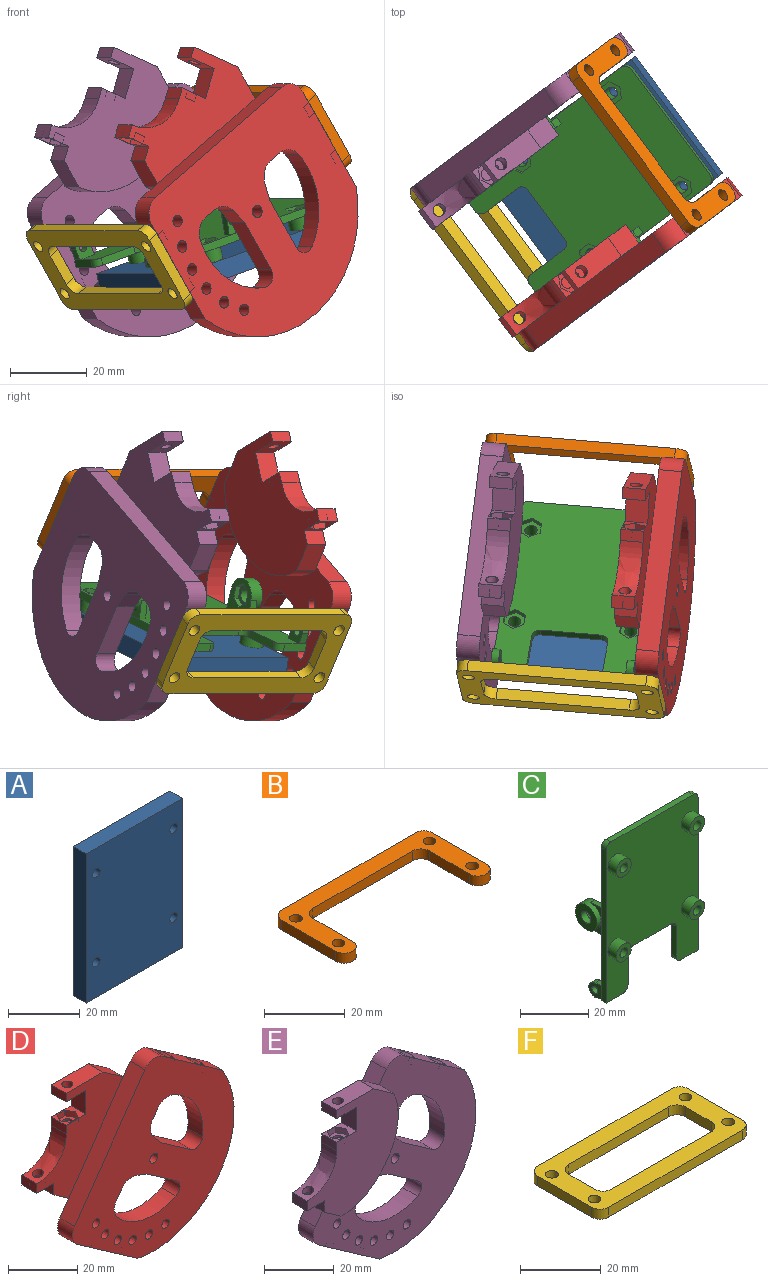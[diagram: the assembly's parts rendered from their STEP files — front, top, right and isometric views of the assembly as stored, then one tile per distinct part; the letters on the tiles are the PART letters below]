
ASSEMBLY  parts=6 mates=5
PART A: 10 faces, bbox 38x5x51 mm
  f0: plane 38x5mm, normal (0,0,1), area 190mm2, adj f1,f7,f8,f9
  f1: plane 51x5mm, normal (-1,0,0), area 255mm2, adj f0,f2,f8,f9
  f2: plane 38x5mm, normal (0,0,-1), area 190mm2, adj f1,f7,f8,f9
  f3: cylinder r=1.5mm len=5mm, axis (0,1,0), area 47.1mm2, adj f8,f9
  f4: cylinder r=1.5mm len=5mm, axis (0,1,0), area 47.1mm2, adj f8,f9
  f5: cylinder r=1.5mm len=5mm, axis (0,1,0), area 47.1mm2, adj f8,f9
  f6: cylinder r=1.5mm len=5mm, axis (0,1,0), area 47.1mm2, adj f8,f9
  f7: plane 51x5mm, normal (1,0,0), area 255mm2, adj f0,f2,f8,f9
  f8: plane 51x38mm, normal (0,-1,0), area 1909.7mm2, adj f0,f1,f2,f3,f4,f5,f6,f7
  f9: plane 51x38mm, normal (0,1,0), area 1909.7mm2, adj f0,f1,f2,f3,f4,f5,f6,f7
PART B: 18 faces, bbox 53x25x3 mm
  f0: cylinder r=3mm len=6mm, axis (0,0,-1), area 28.3mm2, adj f1,f15,f16,f17
  f1: plane 19x3mm, normal (1,0,0), area 57mm2, adj f0,f2,f16,f17
  f2: cylinder r=3mm len=3mm, axis (0,0,-1), area 14.1mm2, adj f1,f3,f16,f17
  f3: plane 47x3mm, normal (0,1,0), area 141mm2, adj f2,f4,f16,f17
  f4: cylinder r=3mm len=3mm, axis (0,0,-1), area 14.1mm2, adj f3,f5,f16,f17
  f5: plane 19x3mm, normal (-1,0,0), area 57mm2, adj f4,f6,f16,f17
  f6: cylinder r=3mm len=6mm, axis (0,0,-1), area 28.3mm2, adj f5,f7,f16,f17
  f7: plane 14x3mm, normal (1,0,0), area 42mm2, adj f6,f8,f16,f17
  f8: cylinder r=3mm len=3mm, axis (0,0,-1), area 14.1mm2, adj f7,f9,f16,f17
  f9: plane 35x3mm, normal (0,-1,0), area 105mm2, adj f8,f10,f16,f17
  f10: cylinder r=3mm len=3mm, axis (0,0,-1), area 14.1mm2, adj f9,f15,f16,f17
  f11: cylinder r=1.6mm len=3.2mm, axis (0,0,-1), area 30.2mm2, adj f16,f17
  f12: cylinder r=1.6mm len=3.2mm, axis (0,0,-1), area 30.2mm2, adj f16,f17
  f13: cylinder r=1.6mm len=3.2mm, axis (0,0,-1), area 30.2mm2, adj f16,f17
  f14: cylinder r=1.6mm len=3.2mm, axis (0,0,-1), area 30.2mm2, adj f16,f17
  f15: plane 14x3mm, normal (-1,0,0), area 42mm2, adj f0,f10,f16,f17
  f16: plane 53x25mm, normal (0,0,1), area 465.1mm2, adj f0,f1,f2,f3,f4,f5,f6,f7
  f17: plane 53x25mm, normal (0,0,-1), area 465.1mm2, adj f0,f1,f2,f3,f4,f5,f6,f7
PART C: 98 faces, bbox 40.8x15x57.5 mm
  f0: plane 7.1x2mm, normal (0,0,-1), area 14.2mm2, adj f1,f2,f7,f74,f94
  f1: plane 57x38.2mm, normal (0,1,0), area 1713.4mm2, adj f0,f3,f4,f6,f7,f8,f22,f23
  f2: plane 57x38.2mm, normal (0,-1,0), area 1754.9mm2, adj f0,f6,f7,f8,f13,f15,f17,f19
  f3: plane 10x5mm, normal (1,0,0), area 15.7mm2, adj f1,f21,f22,f23
  f4: plane 5.54x5.5mm, normal (1,0,0), area 20mm2, adj f1,f25,f26,f27,f28,f29
  f5: cylinder r=2mm len=4mm, axis (1,0,0), area 27mm2, adj f31,f32
  f6: plane 34.2x2mm, normal (0,0,1), area 68.4mm2, adj f1,f2,f96,f97
  f7: plane 55x2mm, normal (-1,0,0), area 110mm2, adj f0,f1,f2,f97
  f8: plane 7.1x2mm, normal (0,0,-1), area 14.2mm2, adj f1,f2,f28,f67,f95
  f9: cylinder r=1.6mm len=4.35mm, axis (0,1,0), area 43.7mm2, adj f20,f54
  f10: cylinder r=1.6mm len=4.35mm, axis (0,1,0), area 43.7mm2, adj f14,f50
  f11: cylinder r=1.6mm len=4.35mm, axis (0,1,0), area 43.7mm2, adj f16,f46
  f12: cylinder r=1.6mm len=4.35mm, axis (0,1,0), area 43.7mm2, adj f18,f42
  f13: cylinder r=3.1mm len=6.2mm, axis (0,1,0), area 68.2mm2, adj f2,f14
  f14: plane 6.2x6.2mm, normal (0,-1,0), area 22.1mm2, adj f10,f13
  f15: cylinder r=3.1mm len=6.2mm, axis (0,1,0), area 68.2mm2, adj f2,f16
  f16: plane 6.2x6.2mm, normal (0,-1,0), area 22.1mm2, adj f11,f15
  f17: cylinder r=3.1mm len=6.2mm, axis (0,1,0), area 68.2mm2, adj f2,f18
  f18: plane 6.2x6.2mm, normal (0,-1,0), area 22.1mm2, adj f12,f17
  f19: cylinder r=3.1mm len=6.2mm, axis (0,1,0), area 68.2mm2, adj f2,f20
  f20: plane 6.2x6.2mm, normal (0,-1,0), area 22.1mm2, adj f9,f19
  f21: cylinder r=4.5mm len=9mm, axis (1,0,0), area 74.9mm2, adj f3,f22,f23,f24,f31
  f22: plane 5x2mm, normal (0,0.1,1), area 10mm2, adj f1,f3,f21,f24
  f23: plane 5x2mm, normal (0,0.1,-1), area 10mm2, adj f1,f3,f21,f24
  f24: plane 10x9.5mm, normal (-1,0,0), area 53.1mm2, adj f1,f21,f22,f23,f33,f34,f35,f36
  f25: plane 2x0.04mm, normal (0,1,0), area 0.1mm2, adj f4,f26,f28,f30
  f26: cylinder r=2.5mm len=5mm, axis (1,0,0), area 15.7mm2, adj f4,f25,f27,f30
  f27: plane 3x2mm, normal (0,0.16,0.99), area 6.1mm2, adj f1,f4,f26,f30
  f28: plane 3x2mm, normal (0,-0.18,-0.98), area 6.1mm2, adj f4,f8,f25,f30
  f29: cylinder r=1.25mm len=2.5mm, axis (1,0,0), area 15.7mm2, adj f4,f30
  f30: plane 5.54x5.5mm, normal (-1,0,0), area 20mm2, adj f1,f25,f26,f27,f28,f29
  f31: plane 9x9mm, normal (1,0,0), area 51.1mm2, adj f5,f21
  f32: plane 6.35x5.5mm, normal (-1,0,0), area 13.6mm2, adj f5,f33,f34,f35,f36,f37,f38
  f33: plane 3.18x1.5mm, normal (0,0,1), area 4.8mm2, adj f24,f32,f34,f38
  f34: plane 2.75x1.59mm, normal (0,0.87,0.5), area 4.8mm2, adj f24,f32,f33,f35
  f35: plane 2.75x1.59mm, normal (0,0.87,-0.5), area 4.8mm2, adj f24,f32,f34,f36
  f36: plane 3.18x1.5mm, normal (0,0,-1), area 4.8mm2, adj f24,f32,f35,f37
  f37: plane 2.75x1.59mm, normal (0,-0.87,-0.5), area 4.8mm2, adj f24,f32,f36,f38
  f38: plane 2.75x1.59mm, normal (0,-0.87,0.5), area 4.8mm2, adj f24,f32,f33,f37
  f39: plane 2.7x1.56mm, normal (0.5,0,-0.87), area 3.6mm2, adj f1,f40,f42,f66
  f40: plane 3.18x1.15mm, normal (1,0,0), area 3.7mm2, adj f1,f39,f41,f42
  f41: plane 2.7x1.56mm, normal (0.5,0,0.87), area 3.6mm2, adj f1,f40,f42,f65
  f42: plane 6.29x5.4mm, normal (0,1,0), area 17.5mm2, adj f12,f39,f40,f41,f64,f65,f66
  f43: plane 2.7x1.56mm, normal (0.5,0,-0.87), area 3.6mm2, adj f1,f44,f46,f63
  f44: plane 3.18x1.15mm, normal (1,0,0), area 3.7mm2, adj f1,f43,f45,f46
  f45: plane 2.7x1.56mm, normal (0.5,0,0.87), area 3.6mm2, adj f1,f44,f46,f62
  f46: plane 6.29x5.4mm, normal (0,1,0), area 17.5mm2, adj f11,f43,f44,f45,f61,f62,f63
  f47: plane 2.7x1.56mm, normal (0.5,0,0.87), area 3.6mm2, adj f1,f49,f50,f60
  f48: plane 2.7x1.56mm, normal (0.5,0,-0.87), area 3.6mm2, adj f1,f49,f50,f59
  f49: plane 3.18x1.15mm, normal (1,0,0), area 3.7mm2, adj f1,f47,f48,f50
  f50: plane 6.29x5.4mm, normal (0,1,0), area 17.5mm2, adj f10,f47,f48,f49,f58,f59,f60
  f51: plane 2.7x1.56mm, normal (0.5,0,-0.87), area 3.6mm2, adj f1,f52,f54,f57
  f52: plane 3.18x1.15mm, normal (1,0,0), area 3.7mm2, adj f1,f51,f53,f54
  f53: plane 2.7x1.56mm, normal (0.5,0,0.87), area 3.6mm2, adj f1,f52,f54,f56
  f54: plane 6.29x5.4mm, normal (0,1,0), area 17.5mm2, adj f9,f51,f52,f53,f55,f56,f57
  f55: plane 3.18x1.15mm, normal (-1,0,0), area 3.7mm2, adj f1,f54,f56,f57
  f56: plane 2.7x1.56mm, normal (-0.5,0,0.87), area 3.6mm2, adj f1,f53,f54,f55
  f57: plane 2.7x1.56mm, normal (-0.5,0,-0.87), area 3.6mm2, adj f1,f51,f54,f55
  f58: plane 3.18x1.15mm, normal (-1,0,0), area 3.7mm2, adj f1,f50,f59,f60
  f59: plane 2.7x1.56mm, normal (-0.5,0,-0.87), area 3.6mm2, adj f1,f48,f50,f58
  f60: plane 2.7x1.56mm, normal (-0.5,0,0.87), area 3.6mm2, adj f1,f47,f50,f58
  f61: plane 3.18x1.15mm, normal (-1,0,0), area 3.7mm2, adj f1,f46,f62,f63
  f62: plane 2.7x1.56mm, normal (-0.5,0,0.87), area 3.6mm2, adj f1,f45,f46,f61
  f63: plane 2.7x1.56mm, normal (-0.5,0,-0.87), area 3.6mm2, adj f1,f43,f46,f61
  f64: plane 3.18x1.15mm, normal (-1,0,0), area 3.7mm2, adj f1,f42,f65,f66
  f65: plane 2.7x1.56mm, normal (-0.5,0,0.87), area 3.6mm2, adj f1,f41,f42,f64
  f66: plane 2.7x1.56mm, normal (-0.5,0,-0.87), area 3.6mm2, adj f1,f39,f42,f64
  f67: plane 55x2mm, normal (1,0,0), area 110mm2, adj f1,f2,f8,f96
  f68: plane 2x0.04mm, normal (0,1,0), area 0.1mm2, adj f70,f72,f73,f74
  f69: cylinder r=1.25mm len=2.5mm, axis (-1,0,0), area 15.7mm2, adj f72,f73
  f70: cylinder r=2.5mm len=5mm, axis (-1,0,0), area 15.7mm2, adj f68,f71,f72,f73
  f71: plane 3x2mm, normal (0,0.16,0.99), area 6.1mm2, adj f1,f70,f72,f73
  f72: plane 5.54x5.5mm, normal (-1,0,0), area 20mm2, adj f1,f68,f69,f70,f71,f74
  f73: plane 5.54x5.5mm, normal (1,0,0), area 20mm2, adj f1,f68,f69,f70,f71,f74
  f74: plane 3x2mm, normal (0,-0.18,-0.98), area 6.1mm2, adj f0,f68,f72,f73
  f75: plane 10x5mm, normal (-1,0,0), area 15.7mm2, adj f1,f77,f78,f79
  f76: cylinder r=2mm len=4mm, axis (-1,0,0), area 27mm2, adj f81,f82
  f77: cylinder r=4.5mm len=9mm, axis (-1,0,0), area 74.9mm2, adj f75,f78,f79,f80,f81
  f78: plane 5x2mm, normal (0,0.1,1), area 10mm2, adj f1,f75,f77,f80
  f79: plane 5x2mm, normal (0,0.1,-1), area 10mm2, adj f1,f75,f77,f80
  f80: plane 10x9.5mm, normal (1,0,0), area 53.1mm2, adj f1,f77,f78,f79,f83,f84,f85,f86
  f81: plane 9x9mm, normal (-1,0,0), area 51.1mm2, adj f76,f77
  f82: plane 6.35x5.5mm, normal (1,0,0), area 13.6mm2, adj f76,f83,f84,f85,f86,f87,f88
  f83: plane 3.18x1.5mm, normal (0,0,1), area 4.8mm2, adj f80,f82,f84,f88
  f84: plane 2.75x1.59mm, normal (0,0.87,0.5), area 4.8mm2, adj f80,f82,f83,f85
  f85: plane 2.75x1.59mm, normal (0,0.87,-0.5), area 4.8mm2, adj f80,f82,f84,f86
  f86: plane 3.18x1.5mm, normal (0,0,-1), area 4.8mm2, adj f80,f82,f85,f87
  f87: plane 2.75x1.59mm, normal (0,-0.87,-0.5), area 4.8mm2, adj f80,f82,f86,f88
  f88: plane 2.75x1.59mm, normal (0,-0.87,0.5), area 4.8mm2, adj f80,f82,f83,f87
  f89: cylinder r=2mm len=2mm, axis (0,1,0), area 6.3mm2, adj f1,f2,f90,f93
  f90: plane 11x2mm, normal (1,0,0), area 22mm2, adj f1,f2,f89,f94
  f91: plane 11x2mm, normal (-1,0,0), area 22mm2, adj f1,f2,f92,f95
  f92: cylinder r=2mm len=2mm, axis (0,1,0), area 6.3mm2, adj f1,f2,f91,f93
  f93: plane 16x2mm, normal (0,0,-1), area 32mm2, adj f1,f2,f89,f92
  f94: cylinder r=2mm len=2mm, axis (0,-1,0), area 6.3mm2, adj f0,f1,f2,f90
  f95: cylinder r=2mm len=2mm, axis (0,1,0), area 6.3mm2, adj f1,f2,f8,f91
  f96: cylinder r=2mm len=2mm, axis (0,-1,0), area 6.3mm2, adj f1,f2,f6,f67
  f97: cylinder r=2mm len=2mm, axis (0,-1,0), area 6.3mm2, adj f1,f2,f6,f7
PART D: 90 faces, bbox 74.4x12x67.9 mm
  f0: cylinder r=1.6mm len=3.2mm, axis (0,0,-1), area 19mm2, adj f6,f55
  f1: plane 37.48x35.19mm, normal (0,-1,0), area 524.2mm2, adj f2,f3,f4,f5,f6,f7,f8,f9
  f2: plane 8x6mm, normal (0,0,-1), area 40mm2, adj f1,f3,f14,f15,f45
  f3: plane 8.3x6mm, normal (-1,0,0), area 49.8mm2, adj f1,f2,f4,f15
  f4: plane 8x6mm, normal (0,0,1), area 21.8mm2, adj f1,f3,f5,f15,f47,f48,f49,f50
  f5: plane 6x3mm, normal (-1,0,0), area 18mm2, adj f1,f4,f6,f15
  f6: extruded ~12x11.61mm, area 103.6mm2, adj f0,f1,f5,f7,f15
  f7: plane 6x3.45mm, normal (-1,0,0), area 20.7mm2, adj f1,f6,f8,f15
  f8: plane 7x6mm, normal (0,0,-1), area 15.8mm2, adj f1,f7,f9,f15,f56,f57,f58,f59
  f9: plane 6x4mm, normal (-1,0,0), area 24mm2, adj f1,f8,f10,f15
  f10: plane 6.69x6mm, normal (-0.57,0,-0.82), area 49mm2, adj f1,f9,f11,f15,f16
  f11: extruded ~32.29x23.23mm, area 272.9mm2, adj f10,f12,f15,f16
  f12: plane 8.19x6mm, normal (0.57,0,0.82), area 60mm2, adj f1,f11,f13,f15
  f13: plane 15x6mm, normal (0,0,1), area 82mm2, adj f1,f12,f14,f15,f45
  f14: plane 6x3mm, normal (-1,0,0), area 18mm2, adj f1,f2,f13,f15
  f15: plane 39.25x38.99mm, normal (0,1,0), area 816.6mm2, adj f2,f3,f4,f5,f6,f7,f8,f9
  f16: plane 67.91x65.92mm, normal (0,1,0), area 1965.6mm2, adj f10,f11,f17,f18,f19,f20,f21,f22
  f17: cylinder r=5mm len=6.08mm, axis (0,1,0), area 39.3mm2, adj f16,f18,f40,f44
  f18: plane 6x2.94mm, normal (0.82,0,-0.57), area 21.5mm2, adj f16,f17,f19,f44
  f19: cylinder r=5mm len=6mm, axis (0,1,0), area 40.5mm2, adj f16,f18,f20,f44
  f20: cylinder r=20mm len=20.9mm, axis (0,1,0), area 156mm2, adj f16,f19,f21,f44
  f21: cylinder r=3mm len=6mm, axis (0,1,0), area 37.1mm2, adj f16,f20,f22,f44
  f22: plane 12.29x8.6mm, normal (0.57,0,0.82), area 90mm2, adj f16,f21,f40,f44
  f23: cylinder r=5mm len=6mm, axis (0,1,0), area 39.3mm2, adj f16,f24,f41,f44
  f24: plane 6x4.43mm, normal (-0.34,0,-0.94), area 28.3mm2, adj f16,f23,f25,f44
  f25: plane 12.29x8.6mm, normal (-0.57,0,-0.82), area 90mm2, adj f16,f24,f26,f44
  f26: cylinder r=3mm len=6mm, axis (0,1,0), area 37.1mm2, adj f16,f25,f27,f44
  f27: cylinder r=20mm len=23.82mm, axis (0,1,0), area 156mm2, adj f16,f26,f28,f44
  f28: cylinder r=5mm len=6.24mm, axis (0,1,0), area 40.5mm2, adj f16,f27,f41,f44
  f29: plane 40.96x28.68mm, normal (-0.82,0,0.57), area 300mm2, adj f1,f16,f30,f42,f44
  f30: cylinder r=5mm len=6.96mm, axis (0,1,0), area 47.1mm2, adj f16,f29,f31,f44
  f31: plane 24.57x17.21mm, normal (-0.57,0,-0.82), area 127.6mm2, adj f16,f30,f32,f44,f76,f77,f78,f79
  f32: cylinder r=32.73mm len=49.8mm, axis (0,1,0), area 455.3mm2, adj f16,f31,f33,f44
  f33: plane 24.57x17.21mm, normal (0.57,0,0.82), area 127.6mm2, adj f16,f32,f42,f44,f62,f63,f64,f65
  f34: cylinder r=1.5mm len=6mm, axis (0,1,0), area 56.5mm2, adj f16,f44
  f35: cylinder r=1.5mm len=6mm, axis (0,1,0), area 56.5mm2, adj f16,f44
  f36: cylinder r=1.5mm len=6mm, axis (0,1,0), area 56.5mm2, adj f16,f44
  f37: cylinder r=1.5mm len=6mm, axis (0,1,0), area 56.5mm2, adj f16,f44
  f38: cylinder r=1.5mm len=6mm, axis (0,1,0), area 56.5mm2, adj f16,f44
  f39: cylinder r=1.6mm len=6mm, axis (0,1,0), area 60.3mm2, adj f16,f44
  f40: plane 6x3.61mm, normal (0.77,0,0.64), area 28.3mm2, adj f16,f17,f22,f44
  f41: plane 6x2.94mm, normal (0.82,0,-0.57), area 21.5mm2, adj f16,f23,f28,f44
  f42: cylinder r=5mm len=6.96mm, axis (0,1,0), area 47.1mm2, adj f16,f29,f33,f44
  f43: cylinder r=1.5mm len=6mm, axis (0,1,0), area 56.5mm2, adj f16,f44
  f44: plane 67.91x65.92mm, normal (0,-1,0), area 2258mm2, adj f17,f18,f19,f20,f21,f22,f23,f24
  f45: cylinder r=1.6mm len=3.2mm, axis (0,0,1), area 30.2mm2, adj f2,f13
  f46: plane 6.35x5.5mm, normal (0,0,1), area 18.2mm2, adj f47,f48,f49,f50,f51,f52,f54
  f47: plane 3.18x2mm, normal (0,1,0), area 6.4mm2, adj f4,f46,f48,f52
  f48: plane 2.75x2mm, normal (-0.87,0.5,0), area 6.4mm2, adj f4,f46,f47,f49
  f49: plane 2.75x2mm, normal (-0.87,-0.5,0), area 6.4mm2, adj f4,f46,f48,f50
  f50: plane 3.18x2mm, normal (0,-1,0), area 6.4mm2, adj f4,f46,f49,f51
  f51: plane 2.75x2mm, normal (0.87,-0.5,0), area 6.4mm2, adj f4,f46,f50,f52
  f52: plane 2.75x2mm, normal (0.87,0.5,0), area 6.4mm2, adj f4,f46,f47,f51
  f53: plane 3.2x3.2mm, normal (0,0,1), area 8mm2, adj f54
  f54: cylinder r=1.6mm len=3.2mm, axis (0,0,1), area 7mm2, adj f46,f53
  f55: plane 6.35x5.5mm, normal (0,0,-1), area 18.2mm2, adj f0,f56,f57,f58,f59,f60,f61
  f56: plane 3.18x2mm, normal (0,-1,0), area 6.4mm2, adj f8,f55,f57,f61
  f57: plane 2.75x2mm, normal (-0.87,-0.5,0), area 6.4mm2, adj f8,f55,f56,f58
  f58: plane 2.75x2mm, normal (-0.87,0.5,0), area 6.4mm2, adj f8,f55,f57,f59
  f59: plane 3.18x2mm, normal (0,1,0), area 6.4mm2, adj f8,f55,f58,f60
  f60: plane 2.75x2mm, normal (0.87,0.5,0), area 6.4mm2, adj f8,f55,f59,f61
  f61: plane 2.75x2mm, normal (0.87,-0.5,0), area 6.4mm2, adj f8,f55,f56,f60
  f62: plane 3.75x3.46mm, normal (0,1,0), area 6.4mm2, adj f33,f63,f67,f68
  f63: plane 2.75x2.55mm, normal (-0.71,0.5,0.5), area 6.4mm2, adj f33,f62,f64,f68
  f64: plane 2.75x2.55mm, normal (-0.71,-0.5,0.5), area 6.4mm2, adj f33,f63,f65,f68
  f65: plane 3.75x3.46mm, normal (0,-1,0), area 6.4mm2, adj f33,f64,f66,f68
  f66: plane 2.75x2.55mm, normal (0.71,-0.5,-0.5), area 6.4mm2, adj f33,f65,f67,f68
  f67: plane 2.75x2.55mm, normal (0.71,0.5,-0.5), area 6.4mm2, adj f33,f62,f66,f68
  f68: plane 5.5x5.2mm, normal (0.57,0,0.82), area 26.2mm2, adj f62,f63,f64,f65,f66,f67
  f69: plane 3.75x3.46mm, normal (0,1,0), area 6.4mm2, adj f33,f70,f74,f75
  f70: plane 2.75x2.55mm, normal (-0.71,0.5,0.5), area 6.4mm2, adj f33,f69,f71,f75
  f71: plane 2.75x2.55mm, normal (-0.71,-0.5,0.5), area 6.4mm2, adj f33,f70,f72,f75
  f72: plane 3.75x3.46mm, normal (0,-1,0), area 6.4mm2, adj f33,f71,f73,f75
  f73: plane 2.75x2.55mm, normal (0.71,-0.5,-0.5), area 6.4mm2, adj f33,f72,f74,f75
  f74: plane 2.75x2.55mm, normal (0.71,0.5,-0.5), area 6.4mm2, adj f33,f69,f73,f75
  f75: plane 5.5x5.2mm, normal (0.57,0,0.82), area 26.2mm2, adj f69,f70,f71,f72,f73,f74
  f76: plane 2.75x2.55mm, normal (0.71,0.5,-0.5), area 6.4mm2, adj f31,f77,f81,f82
  f77: plane 2.75x2.55mm, normal (0.71,-0.5,-0.5), area 6.4mm2, adj f31,f76,f78,f82
  f78: plane 3.75x3.46mm, normal (0,-1,0), area 6.4mm2, adj f31,f77,f79,f82
  f79: plane 2.75x2.55mm, normal (-0.71,-0.5,0.5), area 6.4mm2, adj f31,f78,f80,f82
  f80: plane 2.75x2.55mm, normal (-0.71,0.5,0.5), area 6.4mm2, adj f31,f79,f81,f82
  f81: plane 3.75x3.46mm, normal (0,1,0), area 6.4mm2, adj f31,f76,f80,f82
  f82: plane 5.5x5.2mm, normal (-0.57,0,-0.82), area 26.2mm2, adj f76,f77,f78,f79,f80,f81
  f83: plane 2.75x2.55mm, normal (0.71,-0.5,-0.5), area 6.4mm2, adj f31,f84,f88,f89
  f84: plane 3.75x3.46mm, normal (0,-1,0), area 6.4mm2, adj f31,f83,f85,f89
  f85: plane 2.75x2.55mm, normal (-0.71,-0.5,0.5), area 6.4mm2, adj f31,f84,f86,f89
  f86: plane 2.75x2.55mm, normal (-0.71,0.5,0.5), area 6.4mm2, adj f31,f85,f87,f89
  f87: plane 3.75x3.46mm, normal (0,1,0), area 6.4mm2, adj f31,f86,f88,f89
  f88: plane 2.75x2.55mm, normal (0.71,0.5,-0.5), area 6.4mm2, adj f31,f83,f87,f89
  f89: plane 5.5x5.2mm, normal (-0.57,0,-0.82), area 26.2mm2, adj f83,f84,f85,f86,f87,f88
PART E: 90 faces, bbox 74.4x12x67.9 mm
  f0: cylinder r=1.6mm len=3.2mm, axis (0,0,-1), area 19.1mm2, adj f6,f55
  f1: plane 37.48x35.19mm, normal (0,1,0), area 524.2mm2, adj f2,f3,f4,f5,f6,f7,f8,f9
  f2: plane 8x6mm, normal (0,0,-1), area 40mm2, adj f1,f3,f14,f15,f45
  f3: plane 8.3x6mm, normal (-1,0,0), area 49.8mm2, adj f1,f2,f4,f15
  f4: plane 8x6mm, normal (0,0,1), area 21.8mm2, adj f1,f3,f5,f15,f47,f48,f49,f50
  f5: plane 6x3mm, normal (-1,0,0), area 18mm2, adj f1,f4,f6,f15
  f6: extruded ~12x11.61mm, area 103.6mm2, adj f0,f1,f5,f7,f15
  f7: plane 6x3.45mm, normal (-1,0,0), area 20.7mm2, adj f1,f6,f8,f15
  f8: plane 7x6mm, normal (0,0,-1), area 15.8mm2, adj f1,f7,f9,f15,f56,f57,f58,f59
  f9: plane 6x4mm, normal (-1,0,0), area 24mm2, adj f1,f8,f10,f15
  f10: plane 6.69x6mm, normal (-0.57,0,-0.82), area 49mm2, adj f1,f9,f11,f15,f16
  f11: extruded ~32.29x23.23mm, area 272.9mm2, adj f10,f12,f15,f16
  f12: plane 8.19x6mm, normal (0.57,0,0.82), area 60mm2, adj f1,f11,f13,f15
  f13: plane 15x6mm, normal (0,0,1), area 82mm2, adj f1,f12,f14,f15,f45
  f14: plane 6x3mm, normal (-1,0,0), area 18mm2, adj f1,f2,f13,f15
  f15: plane 39.25x38.99mm, normal (0,-1,0), area 816.6mm2, adj f2,f3,f4,f5,f6,f7,f8,f9
  f16: plane 67.91x65.92mm, normal (0,-1,0), area 1965.6mm2, adj f10,f11,f17,f18,f19,f20,f21,f22
  f17: cylinder r=5mm len=6.08mm, axis (0,-1,0), area 39.3mm2, adj f16,f18,f40,f44
  f18: plane 6x2.94mm, normal (0.82,0,-0.57), area 21.5mm2, adj f16,f17,f19,f44
  f19: cylinder r=5mm len=6mm, axis (0,-1,0), area 40.5mm2, adj f16,f18,f20,f44
  f20: cylinder r=20mm len=20.9mm, axis (0,-1,0), area 156mm2, adj f16,f19,f21,f44
  f21: cylinder r=3mm len=6mm, axis (0,-1,0), area 37.1mm2, adj f16,f20,f22,f44
  f22: plane 12.29x8.6mm, normal (0.57,0,0.82), area 90mm2, adj f16,f21,f40,f44
  f23: cylinder r=5mm len=6mm, axis (0,-1,0), area 39.3mm2, adj f16,f24,f41,f44
  f24: plane 6x4.43mm, normal (-0.34,0,-0.94), area 28.3mm2, adj f16,f23,f25,f44
  f25: plane 12.29x8.6mm, normal (-0.57,0,-0.82), area 90mm2, adj f16,f24,f26,f44
  f26: cylinder r=3mm len=6mm, axis (0,-1,0), area 37.1mm2, adj f16,f25,f27,f44
  f27: cylinder r=20mm len=23.82mm, axis (0,-1,0), area 156mm2, adj f16,f26,f28,f44
  f28: cylinder r=5mm len=6.24mm, axis (0,-1,0), area 40.5mm2, adj f16,f27,f41,f44
  f29: plane 40.96x28.68mm, normal (-0.82,0,0.57), area 300mm2, adj f1,f16,f30,f42,f44
  f30: cylinder r=5mm len=6.96mm, axis (0,-1,0), area 47.1mm2, adj f16,f29,f31,f44
  f31: plane 24.57x17.21mm, normal (-0.57,0,-0.82), area 127.6mm2, adj f16,f30,f32,f44,f76,f77,f78,f79
  f32: cylinder r=32.73mm len=49.8mm, axis (0,-1,0), area 455.3mm2, adj f16,f31,f33,f44
  f33: plane 24.57x17.21mm, normal (0.57,0,0.82), area 127.6mm2, adj f16,f32,f42,f44,f62,f63,f64,f65
  f34: cylinder r=1.5mm len=6mm, axis (0,-1,0), area 56.5mm2, adj f16,f44
  f35: cylinder r=1.5mm len=6mm, axis (0,-1,0), area 56.5mm2, adj f16,f44
  f36: cylinder r=1.5mm len=6mm, axis (0,-1,0), area 56.5mm2, adj f16,f44
  f37: cylinder r=1.5mm len=6mm, axis (0,-1,0), area 56.5mm2, adj f16,f44
  f38: cylinder r=1.5mm len=6mm, axis (0,-1,0), area 56.5mm2, adj f16,f44
  f39: cylinder r=1.6mm len=6mm, axis (0,-1,0), area 60.3mm2, adj f16,f44
  f40: plane 6x3.61mm, normal (0.77,0,0.64), area 28.3mm2, adj f16,f17,f22,f44
  f41: plane 6x2.94mm, normal (0.82,0,-0.57), area 21.5mm2, adj f16,f23,f28,f44
  f42: cylinder r=5mm len=6.96mm, axis (0,-1,0), area 47.1mm2, adj f16,f29,f33,f44
  f43: cylinder r=1.5mm len=6mm, axis (0,-1,0), area 56.5mm2, adj f16,f44
  f44: plane 67.91x65.92mm, normal (0,1,0), area 2258mm2, adj f17,f18,f19,f20,f21,f22,f23,f24
  f45: cylinder r=1.6mm len=3.2mm, axis (0,0,1), area 30.2mm2, adj f2,f13
  f46: plane 6.35x5.5mm, normal (0,0,1), area 18.2mm2, adj f47,f48,f49,f50,f51,f52,f54
  f47: plane 3.18x2mm, normal (0,-1,0), area 6.4mm2, adj f4,f46,f48,f52
  f48: plane 2.75x2mm, normal (-0.87,-0.5,0), area 6.4mm2, adj f4,f46,f47,f49
  f49: plane 2.75x2mm, normal (-0.87,0.5,0), area 6.4mm2, adj f4,f46,f48,f50
  f50: plane 3.18x2mm, normal (0,1,0), area 6.4mm2, adj f4,f46,f49,f51
  f51: plane 2.75x2mm, normal (0.87,0.5,0), area 6.4mm2, adj f4,f46,f50,f52
  f52: plane 2.75x2mm, normal (0.87,-0.5,0), area 6.4mm2, adj f4,f46,f47,f51
  f53: plane 3.2x3.2mm, normal (0,0,1), area 8mm2, adj f54
  f54: cylinder r=1.6mm len=3.2mm, axis (0,0,1), area 7mm2, adj f46,f53
  f55: plane 6.35x5.5mm, normal (0,0,-1), area 18.2mm2, adj f0,f56,f57,f58,f59,f60,f61
  f56: plane 3.18x2mm, normal (0,1,0), area 6.4mm2, adj f8,f55,f57,f61
  f57: plane 2.75x2mm, normal (-0.87,0.5,0), area 6.4mm2, adj f8,f55,f56,f58
  f58: plane 2.75x2mm, normal (-0.87,-0.5,0), area 6.4mm2, adj f8,f55,f57,f59
  f59: plane 3.18x2mm, normal (0,-1,0), area 6.4mm2, adj f8,f55,f58,f60
  f60: plane 2.75x2mm, normal (0.87,-0.5,0), area 6.4mm2, adj f8,f55,f59,f61
  f61: plane 2.75x2mm, normal (0.87,0.5,0), area 6.4mm2, adj f8,f55,f56,f60
  f62: plane 3.75x3.46mm, normal (0,-1,0), area 6.4mm2, adj f33,f63,f67,f68
  f63: plane 2.75x2.55mm, normal (-0.71,-0.5,0.5), area 6.4mm2, adj f33,f62,f64,f68
  f64: plane 2.75x2.55mm, normal (-0.71,0.5,0.5), area 6.4mm2, adj f33,f63,f65,f68
  f65: plane 3.75x3.46mm, normal (0,1,0), area 6.4mm2, adj f33,f64,f66,f68
  f66: plane 2.75x2.55mm, normal (0.71,0.5,-0.5), area 6.4mm2, adj f33,f65,f67,f68
  f67: plane 2.75x2.55mm, normal (0.71,-0.5,-0.5), area 6.4mm2, adj f33,f62,f66,f68
  f68: plane 5.5x5.2mm, normal (0.57,0,0.82), area 26.2mm2, adj f62,f63,f64,f65,f66,f67
  f69: plane 3.75x3.46mm, normal (0,-1,0), area 6.4mm2, adj f33,f70,f74,f75
  f70: plane 2.75x2.55mm, normal (-0.71,-0.5,0.5), area 6.4mm2, adj f33,f69,f71,f75
  f71: plane 2.75x2.55mm, normal (-0.71,0.5,0.5), area 6.4mm2, adj f33,f70,f72,f75
  f72: plane 3.75x3.46mm, normal (0,1,0), area 6.4mm2, adj f33,f71,f73,f75
  f73: plane 2.75x2.55mm, normal (0.71,0.5,-0.5), area 6.4mm2, adj f33,f72,f74,f75
  f74: plane 2.75x2.55mm, normal (0.71,-0.5,-0.5), area 6.4mm2, adj f33,f69,f73,f75
  f75: plane 5.5x5.2mm, normal (0.57,0,0.82), area 26.2mm2, adj f69,f70,f71,f72,f73,f74
  f76: plane 2.75x2.55mm, normal (0.71,-0.5,-0.5), area 6.4mm2, adj f31,f77,f81,f82
  f77: plane 2.75x2.55mm, normal (0.71,0.5,-0.5), area 6.4mm2, adj f31,f76,f78,f82
  f78: plane 3.75x3.46mm, normal (0,1,0), area 6.4mm2, adj f31,f77,f79,f82
  f79: plane 2.75x2.55mm, normal (-0.71,0.5,0.5), area 6.4mm2, adj f31,f78,f80,f82
  f80: plane 2.75x2.55mm, normal (-0.71,-0.5,0.5), area 6.4mm2, adj f31,f79,f81,f82
  f81: plane 3.75x3.46mm, normal (0,-1,0), area 6.4mm2, adj f31,f76,f80,f82
  f82: plane 5.5x5.2mm, normal (-0.57,0,-0.82), area 26.2mm2, adj f76,f77,f78,f79,f80,f81
  f83: plane 2.75x2.55mm, normal (0.71,0.5,-0.5), area 6.4mm2, adj f31,f84,f88,f89
  f84: plane 3.75x3.46mm, normal (0,1,0), area 6.4mm2, adj f31,f83,f85,f89
  f85: plane 2.75x2.55mm, normal (-0.71,0.5,0.5), area 6.4mm2, adj f31,f84,f86,f89
  f86: plane 2.75x2.55mm, normal (-0.71,-0.5,0.5), area 6.4mm2, adj f31,f85,f87,f89
  f87: plane 3.75x3.46mm, normal (0,-1,0), area 6.4mm2, adj f31,f86,f88,f89
  f88: plane 2.75x2.55mm, normal (0.71,-0.5,-0.5), area 6.4mm2, adj f31,f83,f87,f89
  f89: plane 5.5x5.2mm, normal (-0.57,0,-0.82), area 26.2mm2, adj f83,f84,f85,f86,f87,f88
PART F: 22 faces, bbox 53x25x3 mm
  f0: plane 19x3mm, normal (1,0,0), area 57mm2, adj f1,f19,f20,f21
  f1: cylinder r=3mm len=3mm, axis (0,0,-1), area 14.1mm2, adj f0,f2,f20,f21
  f2: plane 47x3mm, normal (0,1,0), area 141mm2, adj f1,f3,f20,f21
  f3: cylinder r=3mm len=3mm, axis (0,0,-1), area 14.1mm2, adj f2,f4,f20,f21
  f4: plane 19x3mm, normal (-1,0,0), area 57mm2, adj f3,f5,f20,f21
  f5: cylinder r=3mm len=3mm, axis (0,0,-1), area 14.1mm2, adj f4,f6,f20,f21
  f6: plane 47x3mm, normal (0,-1,0), area 141mm2, adj f5,f19,f20,f21
  f7: cylinder r=3mm len=3mm, axis (0,0,-1), area 14.1mm2, adj f8,f18,f20,f21
  f8: plane 35x3mm, normal (0,-1,0), area 105mm2, adj f7,f9,f20,f21
  f9: cylinder r=3mm len=3mm, axis (0,0,-1), area 14.1mm2, adj f8,f10,f20,f21
  f10: plane 9x3mm, normal (-1,0,0), area 27mm2, adj f9,f11,f20,f21
  f11: cylinder r=3mm len=3mm, axis (0,0,-1), area 14.1mm2, adj f10,f12,f20,f21
  f12: plane 35x3mm, normal (0,1,0), area 105mm2, adj f11,f13,f20,f21
  f13: cylinder r=3mm len=3mm, axis (0,0,-1), area 14.1mm2, adj f12,f18,f20,f21
  f14: cylinder r=1.6mm len=3.2mm, axis (0,0,-1), area 30.2mm2, adj f20,f21
  f15: cylinder r=1.6mm len=3.2mm, axis (0,0,-1), area 30.2mm2, adj f20,f21
  f16: cylinder r=1.6mm len=3.2mm, axis (0,0,-1), area 30.2mm2, adj f20,f21
  f17: cylinder r=1.6mm len=3.2mm, axis (0,0,-1), area 30.2mm2, adj f20,f21
  f18: plane 9x3mm, normal (1,0,0), area 27mm2, adj f7,f13,f20,f21
  f19: cylinder r=3mm len=3mm, axis (0,0,-1), area 14.1mm2, adj f0,f6,f20,f21
  f20: plane 53x25mm, normal (0,0,1), area 677.8mm2, adj f0,f1,f2,f3,f4,f5,f6,f7
  f21: plane 53x25mm, normal (0,0,-1), area 677.8mm2, adj f0,f1,f2,f3,f4,f5,f6,f7
PLACE A rot(axis=(-0.77,0.38,-0.51),88.7deg) t=(-3.82,50.42,-29.22)mm
PLACE B rot(axis=(0.23,0.45,0.86),133.1deg) t=(21.08,12.04,-11.93)mm
PLACE C rot(axis=(0.29,0.57,0.77),137.9deg) t=(-12.95,19.6,-25.82)mm
PLACE D rot(axis=(-0.15,0.46,0.87),41.6deg) t=(-23.17,-5.98,17.42)mm fixed
PLACE E rot(axis=(-0.15,0.46,0.87),41.6deg) t=(-40.51,17.27,17.42)mm
PLACE F rot(axis=(-0.68,0.34,-0.65),75.1deg) t=(-51.97,23.69,-48.06)mm
MATE revolute D.f20 <-> C.f76  axis (-0.6,0.8,0) through (-5.93,-0.61,-22.5)mm
MATE fastened C.f11 <-> A.f4  axis (0.23,0.17,-0.96) through (9.13,17.04,-26.81)mm
MATE fastened F.f15 <-> E.f31  axis (0.66,0.49,0.57) through (-57.4,15.9,-29.96)mm
MATE fastened B.f11 <-> D.f33  axis (-0.66,-0.49,-0.57) through (10.09,7.59,4.46)mm
MATE fastened D.f89 <-> F.f17  axis (-0.66,-0.49,-0.57) through (-28,-20.8,-28.81)mm
